# Revit family: Legrand Coffret Plexo³ 18 modules
name_source: partatom
category: Equipement électrique
revit_build: Autodesk Revit 2018 (Build: 20170223_1515(x64)
units: mm (PartAtom-declared; Revit-internal decimal feet)

## family parameters
Basée sur le plan de construction = Non
Configuration du panneau = Deux colonnes, circuits au sein
Cote de connecteur circulaire = Utiliser le diamètre
Couper avec des vides une fois chargée = Non
Numéro OmniClass = 23.80.30.11.17
Partagée = Non
Point de calcul de pièce = Non
Titre OmniClass = Distribution Boards and Control Panels
Toujours verticalement = Oui
Type d'élément = Tableau de raccordement

## types (18) — shared parameters
Coffret 601835 = Non
Conditions Générale d'Utilisation = https://export.legrand.com
ETIM Class 6.0 = EC000214
Fabricant = Legrand
IK = 09
IP = 65
Image du type = plexo3_18_rangees_001926_pw_174335_pz_0.jpg
Matière = Polystyrène
RAL = 7046
URL = www.legrand.fr

## per-type parameters (varying)
| type | Bornier N | Bornier T | Coffret 001924 | Coffret 001925 | Coffret 001926 | Coffret 001927 | Coffret 601836 | Coffret 601837 | Coffret 601838 | Coffret 601946 | Coffret 601947 | Coffret 601948 | Coffret 601965 | Coffret 601966 | Coffret 601967 | Coffret 601968 | Coffret 601985 | Coffret 601986 | Coffret 601987 | Coffret 601988 |
| Plexo³ 18 modules 1 rangée 001924 |  | Bornier 5+18 trous | Oui | Non | Non | Non | Non | Non | Non | Non | Non | Non | Non | Non | Non | Non | Non | Non | Non | Non |
| Plexo³ 18 modules 2 rangées 001925 |  | Bornier 5+27 trous | Non | Oui | Non | Non | Non | Non | Non | Non | Non | Non | Non | Non | Non | Non | Non | Non | Non | Non |
| Plexo³ 18 modules 3 rangées 001926 |  | Bornier 5+36 trous | Non | Non | Oui | Non | Non | Non | Non | Non | Non | Non | Non | Non | Non | Non | Non | Non | Non | Non |
| Plexo³ 18 modules 4 rangées 001927 |  | Bornier 5+45 trous | Non | Non | Non | Oui | Non | Non | Non | Non | Non | Non | Non | Non | Non | Non | Non | Non | Non | Non |
| Plexo³ 18 modules 1 rangée 601965 |  | Bornier 17 trous | Non | Non | Non | Non | Non | Non | Non | Non | Non | Non | Oui | Non | Non | Non | Non | Non | Non | Non |
| Plexo³ 18 modules 1 rangée 601985 | Bornier 17 trous | Bornier 17 trous | Non | Non | Non | Non | Non | Non | Non | Non | Non | Non | Non | Non | Non | Non | Oui | Non | Non | Non |
| Plexo³ 18 modules 2 rangées 601836 |  |  | Non | Non | Non | Non | Oui | Non | Non | Non | Non | Non | Non | Non | Non | Non | Non | Non | Non | Non |
| Plexo³ 18 modules 2 rangées 601946 |  |  | Non | Non | Non | Non | Non | Non | Non | Oui | Non | Non | Non | Non | Non | Non | Non | Non | Non | Non |
| Plexo³ 18 modules 2 rangées 601966 |  | Bornier 22 trous | Non | Non | Non | Non | Non | Non | Non | Non | Non | Non | Non | Oui | Non | Non | Non | Non | Non | Non |
| Plexo³ 18 modules 2 rangées 601986 | Bornier 22 trous | Bornier 22 trous | Non | Non | Non | Non | Non | Non | Non | Non | Non | Non | Non | Non | Non | Non | Non | Oui | Non | Non |
| Plexo³ 18 modules 3 rangées 601947 |  |  | Non | Non | Non | Non | Non | Non | Non | Non | Oui | Non | Non | Non | Non | Non | Non | Non | Non | Non |
| Plexo³ 18 modules 3 rangées 601967 |  | Bornier 27 trous | Non | Non | Non | Non | Non | Non | Non | Non | Non | Non | Non | Non | Oui | Non | Non | Non | Non | Non |
| Plexo³ 18 modules 3 rangées 601987 | Bornier 27 trous | Bornier 27 trous | Non | Non | Non | Non | Non | Non | Non | Non | Non | Non | Non | Non | Non | Non | Non | Non | Oui | Non |
| Plexo³ 18 modules 4 rangées 601838 |  |  | Non | Non | Non | Non | Non | Non | Oui | Non | Non | Non | Non | Non | Non | Non | Non | Non | Non | Non |
| Plexo³ 18 modules 4 rangées 601948 |  |  | Non | Non | Non | Non | Non | Non | Non | Non | Non | Oui | Non | Non | Non | Non | Non | Non | Non | Non |
| Plexo³ 18 modules 4 rangées 601968 |  | Bornier 35 trous | Non | Non | Non | Non | Non | Non | Non | Non | Non | Non | Non | Non | Non | Oui | Non | Non | Non | Non |
| Plexo³ 18 modules 4 rangées 601988 | Bornier 35 trous | Bornier 35 trous | Non | Non | Non | Non | Non | Non | Non | Non | Non | Non | Non | Non | Non | Non | Non | Non | Non | Oui |
| Plexo³ 18 modules 3 rangées 601837 |  |  | Non | Non | Non | Non | Non | Oui | Non | Non | Non | Non | Non | Non | Non | Non | Non | Non | Non | Non |

note: column(s) folded — value = type name in every type: Description
